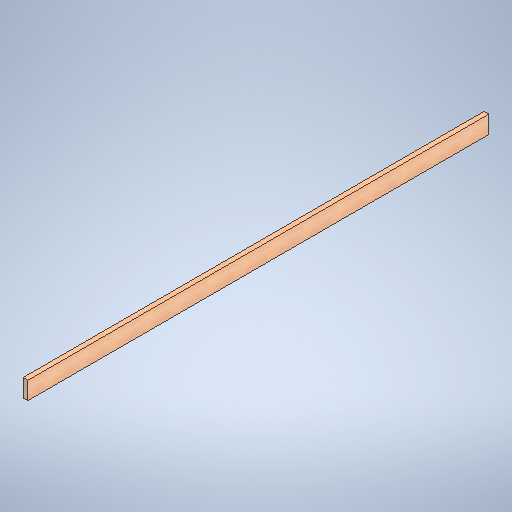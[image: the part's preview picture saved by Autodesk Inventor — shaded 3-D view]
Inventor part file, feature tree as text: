
AUTODESK INVENTOR PART (.ipt)
format: ipt  version: 2025 (Build 290162010, 162A)  size: 275,968 bytes
history: native  units: in
note: dims shown in document units (in); Inventor stores cm internally (conversion verified against a paired STEP export)
features: extrude x1, sketch x1
ambient origin geometry x8: Origin, YZ Plane, XZ Plane, XY Plane, X Axis, Y Axis, Z Axis, Center Point
bodies: Solid1 (feature_tree)
feature tree (2):
  extrude  "Extrusion1"  Depth=5.5in
  sketch  "Sketch1"  dims[d0=1.5in d1=5.5in d2=144.0in d3=0.0in]
